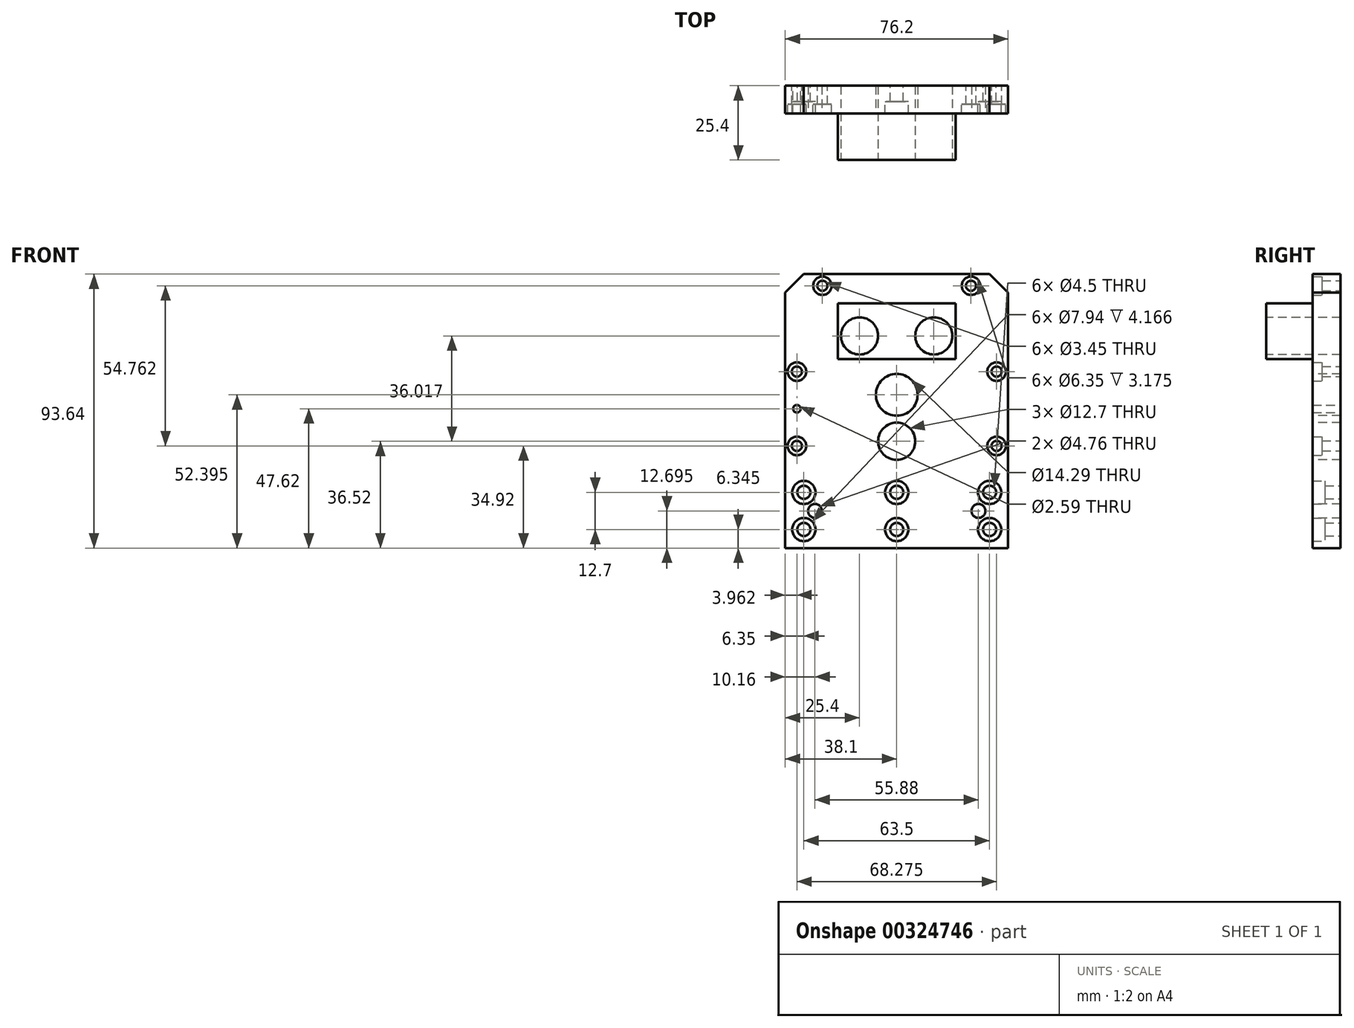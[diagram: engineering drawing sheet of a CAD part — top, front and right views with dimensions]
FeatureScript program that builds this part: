
annotation { "Feature Type Name" : "Feature", "Feature Type Description" : "" }
export const myFeature = defineFeature(function(context is Context, id is Id, definition is map)
    precondition{}
    {
        {
            var Q0;
            Q0=qCreatedBy(makeId("Front.planeOp"),FACE);
            var sketch = newSketch(context, id + "F0", { "sketchPlane" : qUnion([Q0])});
            skLineSegment(sketch, "E0.bottom", {"start": v(-38.1, 46.82) * mm, "end": v(38.1, 46.82) * mm});
            skLineSegment(sketch, "E0.top", {"start": v(-38.1, -46.82) * mm, "end": v(38.1, -46.82) * mm});
            skLineSegment(sketch, "E0.left", {"start": v(-38.1, 46.82) * mm, "end": v(-38.1, -46.82) * mm});
            skLineSegment(sketch, "E0.right", {"start": v(38.1, 46.82) * mm, "end": v(38.1, -46.82) * mm});
            skPoint(sketch, "E0.middle", {"position": v(0, 0) * mm});
            skSolve(sketch);
        }
        {
            var Q0;
            Q0=makeQuery(id+"F0.imprint","IMPRINT",FACE,{"disambiguationData":[TD([[makeQuery(id+"F0.imprint","IMPRINT",EDGE,{"derivedFrom":sQuery(id+"F0.wireOp",EDGE,"E0.bottom")}),-1.0]])]});
            extrude(context, id + "F1", {"entities" : qUnion([Q0]), "depth" : 9.52 * mm});
        }
        {
            var Q0;
            Q0=makeQuery(id+"F1.opExtrude","CAP_FACE",FACE,{"disambiguationData":[OSD([sQuery(id+"F0.wireOp",EDGE,"E0.bottom"),sQuery(id+"F0.wireOp",EDGE,"E0.top"),sQuery(id+"F0.wireOp",EDGE,"E0.left"),sQuery(id+"F0.wireOp",EDGE,"E0.right")])],"isStart":false});
            var sketch = newSketch(context, id + "F2", { "sketchPlane" : qUnion([Q0])});
            skLineSegment(sketch, "E1.bottom", {"start": v(-20.13, 36.82) * mm, "end": v(20.13, 36.82) * mm});
            skLineSegment(sketch, "E1.top", {"start": v(-20.13, 17.77) * mm, "end": v(20.13, 17.77) * mm});
            skLineSegment(sketch, "E1.left", {"start": v(-20.13, 36.82) * mm, "end": v(-20.13, 17.77) * mm});
            skLineSegment(sketch, "E1.right", {"start": v(20.13, 36.82) * mm, "end": v(20.13, 17.77) * mm});
            skSolve(sketch);
        }
        {
            var Q0;
            Q0=makeQuery(id+"F2.imprint","IMPRINT",FACE,{"disambiguationData":[TD([[makeQuery(id+"F2.imprint","IMPRINT",EDGE,{"derivedFrom":sQuery(id+"F2.wireOp",EDGE,"E1.bottom")}),-1.0]])]});
            extrude(context, id + "F3", {"entities" : qUnion([Q0]), "operationType" : NewBodyOperationType.ADD, "depth" : 15.88 * mm});
        }
        {
            var Q0;
            Q0=makeQuery(id+"F1.opExtrude","CAP_FACE",FACE,{"disambiguationData":[OSD([sQuery(id+"F0.wireOp",EDGE,"E0.bottom"),sQuery(id+"F0.wireOp",EDGE,"E0.top"),sQuery(id+"F0.wireOp",EDGE,"E0.left"),sQuery(id+"F0.wireOp",EDGE,"E0.right")])],"isStart":false});
            var sketch = newSketch(context, id + "F4", { "sketchPlane" : qUnion([Q0])});
            skCircle(sketch, "E2", {"center": v(0, 5.58) * mm, "radius": 7.14 * mm});
            skSolve(sketch);
        }
        {
            var Q0;
            Q0=makeQuery(id+"F4.imprint","IMPRINT",FACE,{"disambiguationData":[TD([[makeQuery(id+"F4.imprint","IMPRINT",EDGE,{"derivedFrom":sQuery(id+"F4.wireOp",EDGE,"E2")}),1.0]])]});
            extrude(context, id + "F5", {"entities" : qUnion([Q0]), "operationType" : NewBodyOperationType.REMOVE, "endBound" : BoundingType.THROUGH_ALL, "oppositeDirection" : true, "depth" : 25.4 * mm});
        }
        {
            var Q0;
            Q0=makeQuery(id+"F1.opExtrude","CAP_FACE",FACE,{"disambiguationData":[OSD([sQuery(id+"F0.wireOp",EDGE,"E0.bottom"),sQuery(id+"F0.wireOp",EDGE,"E0.top"),sQuery(id+"F0.wireOp",EDGE,"E0.left"),sQuery(id+"F0.wireOp",EDGE,"E0.right")])],"isStart":false});
            var sketch = newSketch(context, id + "F6", { "sketchPlane" : qUnion([Q0])});
            skCircle(sketch, "E3", {"center": v(0, -10.3) * mm, "radius": 6.35 * mm});
            skSolve(sketch);
        }
        {
            var Q0;
            Q0=makeQuery(id+"F6.imprint","IMPRINT",FACE,{"disambiguationData":[TD([[makeQuery(id+"F6.imprint","IMPRINT",EDGE,{"derivedFrom":sQuery(id+"F6.wireOp",EDGE,"E3")}),1.0]])]});
            extrude(context, id + "F7", {"entities" : qUnion([Q0]), "operationType" : NewBodyOperationType.REMOVE, "endBound" : BoundingType.THROUGH_ALL, "oppositeDirection" : true, "depth" : 25.4 * mm});
        }
        {
            var Q0;
            Q0=makeQuery(id+"F3.opExtrude","CAP_FACE",FACE,{"disambiguationData":[OSD([sQuery(id+"F2.wireOp",EDGE,"E1.bottom"),sQuery(id+"F2.wireOp",EDGE,"E1.top"),sQuery(id+"F2.wireOp",EDGE,"E1.left"),sQuery(id+"F2.wireOp",EDGE,"E1.right")])],"isStart":false});
            var sketch = newSketch(context, id + "F8", { "sketchPlane" : qUnion([Q0])});
            skCircle(sketch, "E4", {"center": v(-12.7, 25.72) * mm, "radius": 6.35 * mm});
            skCircle(sketch, "E5", {"center": v(12.7, 25.72) * mm, "radius": 6.35 * mm});
            skSolve(sketch);
        }
        {
            var Q0;
            Q0=makeQuery(id+"F8.imprint","IMPRINT",FACE,{"disambiguationData":[TD([[makeQuery(id+"F8.imprint","IMPRINT",EDGE,{"derivedFrom":sQuery(id+"F8.wireOp",EDGE,"E4")}),1.0]])]});
            var Q1;
            Q1=makeQuery(id+"F8.imprint","IMPRINT",FACE,{"disambiguationData":[TD([[makeQuery(id+"F8.imprint","IMPRINT",EDGE,{"derivedFrom":sQuery(id+"F8.wireOp",EDGE,"E5")}),1.0]])]});
            extrude(context, id + "F9", {"entities" : qUnion([Q0, Q1]), "operationType" : NewBodyOperationType.REMOVE, "endBound" : BoundingType.THROUGH_ALL, "oppositeDirection" : true, "depth" : 25.4 * mm});
        }
        {
            var Q0;
            Q0=makeQuery(id+"F1.opExtrude","CAP_FACE",FACE,{"disambiguationData":[OSD([sQuery(id+"F0.wireOp",EDGE,"E0.bottom"),sQuery(id+"F0.wireOp",EDGE,"E0.top"),sQuery(id+"F0.wireOp",EDGE,"E0.left"),sQuery(id+"F0.wireOp",EDGE,"E0.right")])],"isStart":false});
            var sketch = newSketch(context, id + "F10", { "sketchPlane" : qUnion([Q0])});
            skCircle(sketch, "E6", {"center": v(-27.94, -34.12) * mm, "radius": 2.38 * mm});
            skCircle(sketch, "E7", {"center": v(27.94, -34.12) * mm, "radius": 2.38 * mm});
            skSolve(sketch);
        }
        {
            var Q0;
            Q0=makeQuery(id+"F10.imprint","IMPRINT",FACE,{"disambiguationData":[TD([[makeQuery(id+"F10.imprint","IMPRINT",EDGE,{"derivedFrom":sQuery(id+"F10.wireOp",EDGE,"E6")}),1.0]])]});
            var Q1;
            Q1=makeQuery(id+"F10.imprint","IMPRINT",FACE,{"disambiguationData":[TD([[makeQuery(id+"F10.imprint","IMPRINT",EDGE,{"derivedFrom":sQuery(id+"F10.wireOp",EDGE,"E7")}),1.0]])]});
            extrude(context, id + "F11", {"entities" : qUnion([Q0, Q1]), "operationType" : NewBodyOperationType.REMOVE, "endBound" : BoundingType.THROUGH_ALL, "oppositeDirection" : true, "depth" : 25.4 * mm});
        }
        {
            var Q0;
            Q0=makeQuery(id+"F1.opExtrude","SWEPT_EDGE",EDGE,{"disambiguationData":[OSD([sQuery(id+"F0.wireOp",EDGE,"E0.bottom"),sQuery(id+"F0.wireOp",EDGE,"E0.right")])]});
            var Q1;
            Q1=makeQuery(id+"F1.opExtrude","SWEPT_EDGE",EDGE,{"disambiguationData":[OSD([sQuery(id+"F0.wireOp",EDGE,"E0.bottom"),sQuery(id+"F0.wireOp",EDGE,"E0.left")])]});
            chamfer(context, id + "F12", {"entities" : qUnion([Q0, Q1]), "width" : 6.35 * mm, "tangentPropagation" : true});
        }
        {
            var Q0;
            Q0=makeQuery(id+"F1.opExtrude","CAP_FACE",FACE,{"disambiguationData":[OSD([sQuery(id+"F0.wireOp",EDGE,"E0.bottom"),sQuery(id+"F0.wireOp",EDGE,"E0.top"),sQuery(id+"F0.wireOp",EDGE,"E0.left"),sQuery(id+"F0.wireOp",EDGE,"E0.right")])],"isStart":false});
            var sketch = newSketch(context, id + "F13", { "sketchPlane" : qUnion([Q0])});
            skPoint(sketch, "E8", {"position": v(-31.75, -40.47) * mm});
            skPoint(sketch, "E9", {"position": v(31.75, -40.47) * mm});
            skPoint(sketch, "E10", {"position": v(31.75, -27.77) * mm});
            skPoint(sketch, "E11", {"position": v(-31.75, -27.77) * mm});
            skPoint(sketch, "E12", {"position": v(0, -27.77) * mm});
            skPoint(sketch, "E13", {"position": v(0, -40.47) * mm});
            skSolve(sketch);
        }
        {
            var Q0;
            Q0=sQuery(id+"F13.wireOp",VERTEX,"E11");
            var Q1;
            Q1=sQuery(id+"F13.wireOp",VERTEX,"E8");
            var Q2;
            Q2=sQuery(id+"F13.wireOp",VERTEX,"E9");
            var Q3;
            Q3=sQuery(id+"F13.wireOp",VERTEX,"E10");
            var Q4;
            Q4=sQuery(id+"F13.wireOp",VERTEX,"E12");
            var Q5;
            Q5=sQuery(id+"F13.wireOp",VERTEX,"E13");
            var Q6;
            Q6=makeQuery(id+"F1.opExtrude","SWEPT_BODY",BODY,{"disambiguationData":[OSD([sQuery(id+"F0.wireOp",EDGE,"E0.bottom"),sQuery(id+"F0.wireOp",EDGE,"E0.top"),sQuery(id+"F0.wireOp",EDGE,"E0.left"),sQuery(id+"F0.wireOp",EDGE,"E0.right")])]});
            hole(context, id + "F14", {"style" : HoleStyle.C_BORE, "endStyle" : HoleEndStyle.THROUGH, "holeDiameter" : 4.5 * mm, "cBoreDiameter" : 7.94 * mm, "cBoreDepth" : 4.17 * mm, "tappedDepth" : 12.7 * mm, "tapClearance" : 3, "locations" : qUnion([Q0, Q1, Q2, Q3, Q4, Q5]), "scope" : qUnion([Q6])});
        }
        {
            var Q0;
            Q0=makeQuery(id+"F1.opExtrude","CAP_FACE",FACE,{"disambiguationData":[OSD([sQuery(id+"F0.wireOp",EDGE,"E0.bottom"),sQuery(id+"F0.wireOp",EDGE,"E0.top"),sQuery(id+"F0.wireOp",EDGE,"E0.left"),sQuery(id+"F0.wireOp",EDGE,"E0.right")])],"isStart":false});
            var sketch = newSketch(context, id + "F15", { "sketchPlane" : qUnion([Q0])});
            skPoint(sketch, "E14", {"position": v(-25.4, 42.86) * mm});
            skPoint(sketch, "E15", {"position": v(25.4, 42.86) * mm});
            skPoint(sketch, "E16", {"position": v(-34.14, 13.5) * mm});
            skPoint(sketch, "E17", {"position": v(-34.14, -11.9) * mm});
            skPoint(sketch, "E18", {"position": v(34.14, -11.9) * mm});
            skPoint(sketch, "E19", {"position": v(34.14, 13.5) * mm});
            skSolve(sketch);
        }
        {
            var Q0;
            Q0=sQuery(id+"F15.wireOp",VERTEX,"E14");
            var Q1;
            Q1=sQuery(id+"F15.wireOp",VERTEX,"E15");
            var Q2;
            Q2=sQuery(id+"F15.wireOp",VERTEX,"E19");
            var Q3;
            Q3=sQuery(id+"F15.wireOp",VERTEX,"E18");
            var Q4;
            Q4=sQuery(id+"F15.wireOp",VERTEX,"E17");
            var Q5;
            Q5=sQuery(id+"F15.wireOp",VERTEX,"E16");
            var Q6;
            Q6=makeQuery(id+"F1.opExtrude","SWEPT_BODY",BODY,{"disambiguationData":[OSD([sQuery(id+"F0.wireOp",EDGE,"E0.bottom"),sQuery(id+"F0.wireOp",EDGE,"E0.top"),sQuery(id+"F0.wireOp",EDGE,"E0.left"),sQuery(id+"F0.wireOp",EDGE,"E0.right")])]});
            hole(context, id + "F16", {"style" : HoleStyle.C_BORE, "endStyle" : HoleEndStyle.THROUGH, "holeDiameter" : 3.45 * mm, "cBoreDiameter" : 6.35 * mm, "cBoreDepth" : 3.17 * mm, "majorDiameter" : 6.35 * mm, "isTappedThrough" : true, "tappedDepth" : 12.7 * mm, "tapClearance" : 3, "locations" : qUnion([Q0, Q1, Q2, Q3, Q4, Q5]), "scope" : qUnion([Q6])});
        }
        {
            var Q0;
            Q0=makeQuery(id+"F1.opExtrude","CAP_FACE",FACE,{"disambiguationData":[OSD([sQuery(id+"F0.wireOp",EDGE,"E0.bottom"),sQuery(id+"F0.wireOp",EDGE,"E0.top"),sQuery(id+"F0.wireOp",EDGE,"E0.left"),sQuery(id+"F0.wireOp",EDGE,"E0.right")])],"isStart":false});
            var sketch = newSketch(context, id + "F17", { "sketchPlane" : qUnion([Q0])});
            skPoint(sketch, "E20", {"position": v(-34.14, 0.8) * mm});
            skSolve(sketch);
        }
        {
            var Q0;
            Q0=sQuery(id+"F17.wireOp",VERTEX,"E20");
            var Q1;
            Q1=makeQuery(id+"F1.opExtrude","SWEPT_BODY",BODY,{"disambiguationData":[OSD([sQuery(id+"F0.wireOp",EDGE,"E0.bottom"),sQuery(id+"F0.wireOp",EDGE,"E0.top"),sQuery(id+"F0.wireOp",EDGE,"E0.left"),sQuery(id+"F0.wireOp",EDGE,"E0.right")])]});
            hole(context, id + "F18", {"style" : HoleStyle.SIMPLE, "endStyle" : HoleEndStyle.THROUGH, "holeDiameter" : 2.6 * mm, "majorDiameter" : 6.35 * mm, "isTappedThrough" : true, "tappedDepth" : 12.7 * mm, "tapClearance" : 3, "locations" : qUnion([Q0]), "scope" : qUnion([Q1])});
        }
    });
